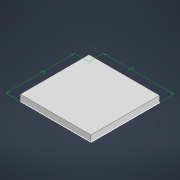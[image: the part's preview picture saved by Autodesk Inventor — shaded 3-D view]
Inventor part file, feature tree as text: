
AUTODESK INVENTOR PART (.ipt)
format: ipt  version: 2022 (Build 260153000, 153)  size: 87,040 bytes
history: native  units: mm
features: other x1, sketch x1, extrude x1
ambient origin geometry x8: Origin, YZ Plane, XZ Plane, XY Plane, X Axis, Y Axis, Z Axis, Center Point
bodies: Body1 (feature_tree)
feature tree (3):
  other  "Твердое тело1"
  sketch  "Эскиз1"
  extrude  "Выдавливание1"  Depth=253.0mm
